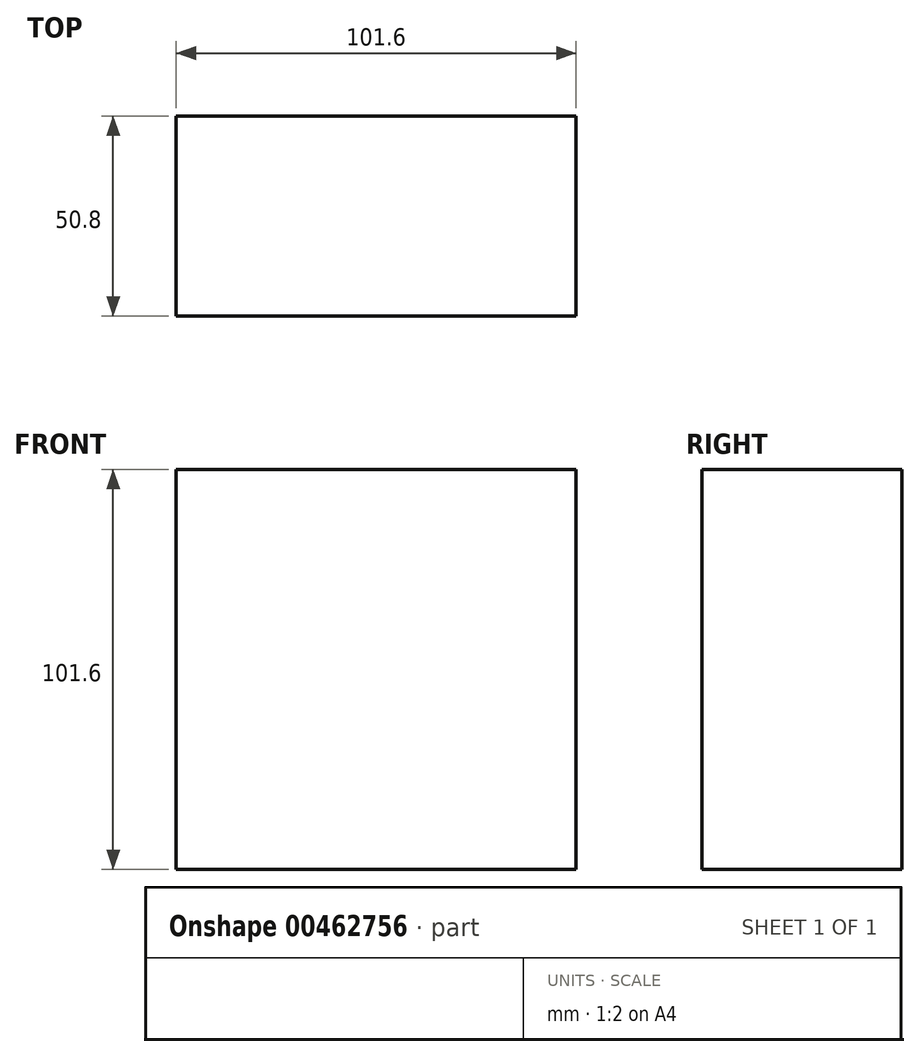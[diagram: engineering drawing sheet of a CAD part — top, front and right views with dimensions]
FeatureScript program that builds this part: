
annotation { "Feature Type Name" : "Feature", "Feature Type Description" : "" }
export const myFeature = defineFeature(function(context is Context, id is Id, definition is map)
    precondition{}
    {
        {
            var Q0;
            Q0=qCreatedBy(makeId("Front.planeOp"),FACE);
            var sketch = newSketch(context, id + "F0", { "sketchPlane" : qUnion([Q0])});
            skLineSegment(sketch, "E0.bottom", {"start": v(50.8, 50.8) * mm, "end": v(-50.8, 50.8) * mm});
            skLineSegment(sketch, "E0.top", {"start": v(50.8, -50.8) * mm, "end": v(-50.8, -50.8) * mm});
            skLineSegment(sketch, "E0.left", {"start": v(50.8, 50.8) * mm, "end": v(50.8, -50.8) * mm});
            skLineSegment(sketch, "E0.right", {"start": v(-50.8, 50.8) * mm, "end": v(-50.8, -50.8) * mm});
            skPoint(sketch, "E0.middle", {"position": v(0, 0) * mm});
            skSolve(sketch);
        }
        {
            var Q0;
            Q0 = qSketchRegion(id + "F0", true);
            extrude(context, id + "F1", {"entities" : qUnion([Q0]), "depth" : 50.8 * mm});
        }
    });
